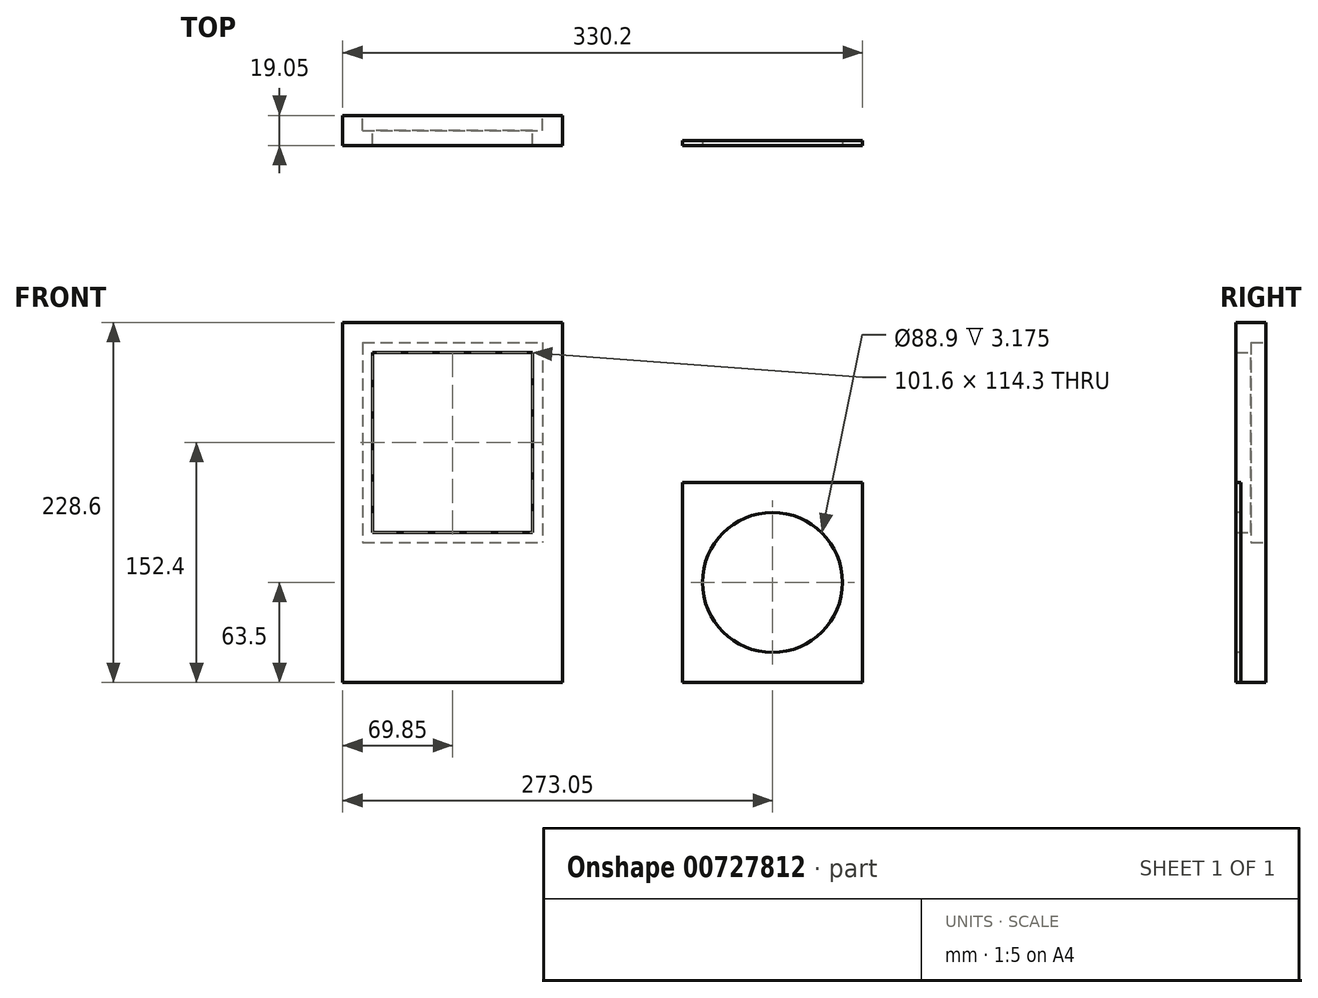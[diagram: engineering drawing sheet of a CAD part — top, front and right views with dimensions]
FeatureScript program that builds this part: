
annotation { "Feature Type Name" : "Feature", "Feature Type Description" : "" }
export const myFeature = defineFeature(function(context is Context, id is Id, definition is map)
    precondition{}
    {
        {
            var Q0;
            Q0=qCreatedBy(makeId("Front.planeOp"),FACE);
            var sketch = newSketch(context, id + "F0", { "sketchPlane" : qUnion([Q0])});
            skLineSegment(sketch, "E0.bottom", {"start": v(0, 0) * mm, "end": v(139.7, 0) * mm});
            skLineSegment(sketch, "E0.top", {"start": v(0, 228.6) * mm, "end": v(139.7, 228.6) * mm});
            skLineSegment(sketch, "E0.left", {"start": v(0, 0) * mm, "end": v(0, 228.6) * mm});
            skLineSegment(sketch, "E0.right", {"start": v(139.7, 0) * mm, "end": v(139.7, 228.6) * mm});
            skSolve(sketch);
        }
        {
            var Q0;
            Q0 = qSketchRegion(id + "F0", true);
            extrude(context, id + "F1", {"entities" : qUnion([Q0]), "oppositeDirection" : true, "depth" : 19.05 * mm, "offsetDistance" : 25.4 * mm});
        }
        {
            var Q0;
            Q0=makeQuery(id+"F1.opExtrude","CAP_FACE",FACE,{"disambiguationData":[OSD([sQuery(id+"F0.wireOp",EDGE,"E0.bottom"),sQuery(id+"F0.wireOp",EDGE,"E0.top"),sQuery(id+"F0.wireOp",EDGE,"E0.left"),sQuery(id+"F0.wireOp",EDGE,"E0.right")])],"isStart":false});
            var sketch = newSketch(context, id + "F2", { "sketchPlane" : qUnion([Q0])});
            skLineSegment(sketch, "E1.bottom", {"start": v(-19.05, 209.55) * mm, "end": v(-120.65, 209.55) * mm});
            skLineSegment(sketch, "E1.top", {"start": v(-19.05, 95.25) * mm, "end": v(-120.65, 95.25) * mm});
            skLineSegment(sketch, "E1.left", {"start": v(-19.05, 209.55) * mm, "end": v(-19.05, 95.25) * mm});
            skLineSegment(sketch, "E1.right", {"start": v(-120.65, 209.55) * mm, "end": v(-120.65, 95.25) * mm});
            skSolve(sketch);
        }
        {
            var Q0;
            Q0 = qSketchRegion(id + "F2", true);
            var Q1;
            Q1=makeQuery(id+"F1.opExtrude","CAP_FACE",FACE,{"disambiguationData":[OSD([sQuery(id+"F0.wireOp",EDGE,"E0.bottom"),sQuery(id+"F0.wireOp",EDGE,"E0.top"),sQuery(id+"F0.wireOp",EDGE,"E0.left"),sQuery(id+"F0.wireOp",EDGE,"E0.right")])],"isStart":true});
            extrude(context, id + "F3", {"entities" : qUnion([Q0, Q1]), "operationType" : NewBodyOperationType.REMOVE, "oppositeDirection" : true, "depth" : 19.05 * mm, "offsetDistance" : 25.4 * mm});
        }
        {
            var Q0;
            Q0=makeQuery(id+"F1.opExtrude","CAP_FACE",FACE,{"disambiguationData":[OSD([sQuery(id+"F0.wireOp",EDGE,"E0.bottom"),sQuery(id+"F0.wireOp",EDGE,"E0.top"),sQuery(id+"F0.wireOp",EDGE,"E0.left"),sQuery(id+"F0.wireOp",EDGE,"E0.right")])],"isStart":false});
            var sketch = newSketch(context, id + "F4", { "sketchPlane" : qUnion([Q0])});
            skLineSegment(sketch, "E2.bottom", {"start": v(-12.7, 215.9) * mm, "end": v(-127, 215.9) * mm});
            skLineSegment(sketch, "E2.top", {"start": v(-12.7, 88.9) * mm, "end": v(-127, 88.9) * mm});
            skLineSegment(sketch, "E2.left", {"start": v(-12.7, 215.9) * mm, "end": v(-12.7, 88.9) * mm});
            skLineSegment(sketch, "E2.right", {"start": v(-127, 215.9) * mm, "end": v(-127, 88.9) * mm});
            skSolve(sketch);
        }
        {
            var Q0;
            Q0 = qSketchRegion(id + "F4", true);
            extrude(context, id + "F5", {"entities" : qUnion([Q0]), "operationType" : NewBodyOperationType.REMOVE, "oppositeDirection" : true, "depth" : 9.52 * mm, "offsetDistance" : 25.4 * mm});
        }
        {
            var Q0;
            Q0=qCreatedBy(makeId("Front.planeOp"),FACE);
            var sketch = newSketch(context, id + "F6", { "sketchPlane" : qUnion([Q0])});
            skLineSegment(sketch, "E3.bottom", {"start": v(215.9, 0) * mm, "end": v(330.2, 0) * mm});
            skLineSegment(sketch, "E3.top", {"start": v(215.9, 127) * mm, "end": v(330.2, 127) * mm});
            skLineSegment(sketch, "E3.left", {"start": v(215.9, 0) * mm, "end": v(215.9, 127) * mm});
            skLineSegment(sketch, "E3.right", {"start": v(330.2, 0) * mm, "end": v(330.2, 127) * mm});
            skSolve(sketch);
        }
        {
            var Q0;
            Q0 = qSketchRegion(id + "F6", true);
            extrude(context, id + "F7", {"entities" : qUnion([Q0]), "oppositeDirection" : true, "depth" : 3.17 * mm, "offsetDistance" : 25.4 * mm});
        }
        {
            var Q0;
            Q0=makeQuery(id+"F7.opExtrude","CAP_FACE",FACE,{"disambiguationData":[OSD([sQuery(id+"F6.wireOp",EDGE,"E3.bottom"),sQuery(id+"F6.wireOp",EDGE,"E3.top"),sQuery(id+"F6.wireOp",EDGE,"E3.left"),sQuery(id+"F6.wireOp",EDGE,"E3.right")])],"isStart":true});
            var sketch = newSketch(context, id + "F8", { "sketchPlane" : qUnion([Q0])});
            skCircle(sketch, "E4", {"center": v(273.05, 63.5) * mm, "radius": 44.45 * mm});
            skPoint(sketch, "E4.centerSnap0", {"position": v(273.05, 127) * mm});
            skSolve(sketch);
        }
        {
            var Q0;
            Q0 = qSketchRegion(id + "F8", true);
            extrude(context, id + "F9", {"entities" : qUnion([Q0]), "operationType" : NewBodyOperationType.REMOVE, "oppositeDirection" : true, "depth" : 25.4 * mm, "offsetDistance" : 25.4 * mm});
        }
    });
